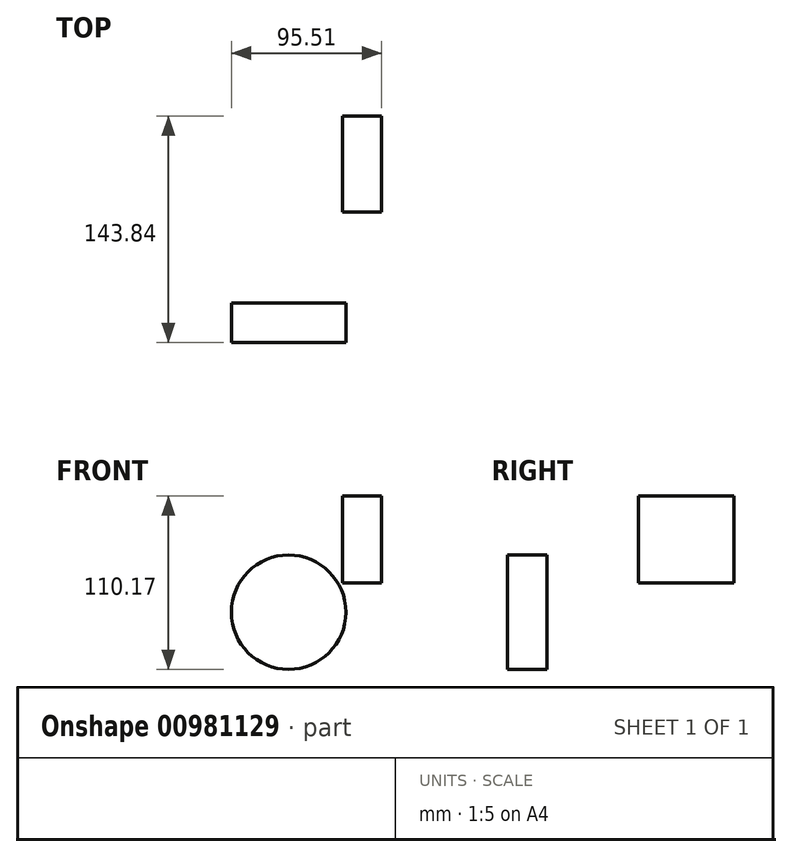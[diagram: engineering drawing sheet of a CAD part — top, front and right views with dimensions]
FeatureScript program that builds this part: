
annotation { "Feature Type Name" : "Feature", "Feature Type Description" : "" }
export const myFeature = defineFeature(function(context is Context, id is Id, definition is map)
    precondition{}
    {
        {
            var Q0;
            Q0=qCreatedBy(makeId("Front.planeOp"),FACE);
            var sketch = newSketch(context, id + "F0", { "sketchPlane" : qUnion([Q0])});
            skCircle(sketch, "E0", {"center": v(-34.14, -40.1) * mm, "radius": 36.37 * mm});
            skSolve(sketch);
        }
        {
            var Q0;
            Q0 = qSketchRegion(id + "F0", true);
            extrude(context, id + "F1", {"entities" : qUnion([Q0]), "depth" : 25 * mm, "offsetDistance" : 25 * mm});
        }
        {
            var Q0;
            Q0=qCreatedBy(makeId("Right.planeOp"),FACE);
            var sketch = newSketch(context, id + "F2", { "sketchPlane" : qUnion([Q0])});
            skLineSegment(sketch, "E1.bottom", {"start": v(118.84, 33.7) * mm, "end": v(57.96, 33.7) * mm});
            skLineSegment(sketch, "E1.top", {"start": v(118.84, -21.37) * mm, "end": v(57.96, -21.37) * mm});
            skLineSegment(sketch, "E1.left", {"start": v(118.84, 33.7) * mm, "end": v(118.84, -21.37) * mm});
            skLineSegment(sketch, "E1.right", {"start": v(57.96, 33.7) * mm, "end": v(57.96, -21.37) * mm});
            skSolve(sketch);
        }
        {
            var Q0;
            Q0 = qSketchRegion(id + "F2", true);
            extrude(context, id + "F3", {"entities" : qUnion([Q0]), "depth" : 25 * mm, "offsetDistance" : 25 * mm});
        }
    });
